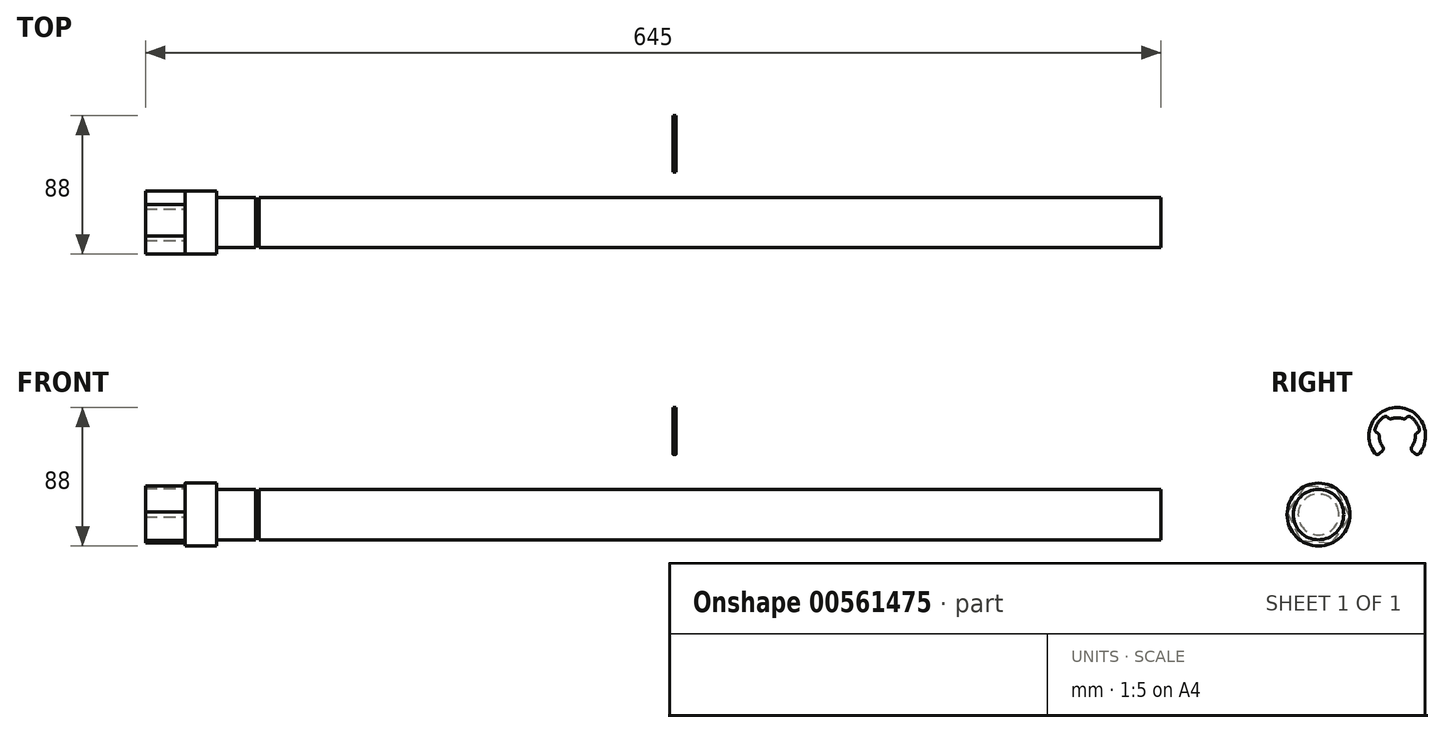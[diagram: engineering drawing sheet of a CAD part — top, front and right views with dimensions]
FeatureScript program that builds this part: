
annotation { "Feature Type Name" : "Feature", "Feature Type Description" : "" }
export const myFeature = defineFeature(function(context is Context, id is Id, definition is map)
    precondition{}
    {
        {
            var Q0;
            Q0=qCreatedBy(makeId("Front.planeOp"),FACE);
            var sketch = newSketch(context, id + "F0", { "sketchPlane" : qUnion([Q0])});
            skLineSegment(sketch, "E0", {"start": v(310, 0) * mm, "end": v(0, 0) * mm});
            skLineSegment(sketch, "E1", {"start": v(0, 0) * mm, "end": v(-310, 0) * mm});
            skLineSegment(sketch, "E2", {"start": v(-310, 0) * mm, "end": v(-310, 20) * mm});
            skLineSegment(sketch, "E3", {"start": v(-310, 20) * mm, "end": v(-290, 20) * mm});
            skLineSegment(sketch, "E4", {"start": v(-290, 20) * mm, "end": v(-290, 16) * mm});
            skLineSegment(sketch, "E5", {"start": v(-290, 16) * mm, "end": v(-265, 16) * mm});
            skLineSegment(sketch, "E6", {"start": v(-265, 16) * mm, "end": v(-265, 13) * mm});
            skLineSegment(sketch, "E7", {"start": v(-265, 13) * mm, "end": v(-263, 13) * mm});
            skLineSegment(sketch, "E8", {"start": v(-263, 13) * mm, "end": v(-263, 16) * mm});
            skLineSegment(sketch, "E9", {"start": v(-263, 16) * mm, "end": v(310, 16) * mm});
            skLineSegment(sketch, "E10", {"start": v(310, 16) * mm, "end": v(310, 0) * mm});
            skLineSegment(sketch, "E11", {"start": v(425.22, 0) * mm, "end": v(-376.8, 0) * mm, "construction": true});
            skPoint(sketch, "E11.startSnap0", {"position": v(155, 0) * mm});
            skSolve(sketch);
        }
        {
            var Q0;
            Q0=makeQuery(id+"F0.imprint","IMPRINT",FACE,{"disambiguationData":[TD([[makeQuery(id+"F0.imprint","IMPRINT",EDGE,{"derivedFrom":sQuery(id+"F0.wireOp",EDGE,"E0")}),-1.0]])]});
            var Q1;
            Q1=sQuery(id+"F0.wireOp",EDGE,"E11");
            revolve(context, id + "F1", {"entities" : qUnion([Q0]), "axis" : qUnion([Q1]), "revolveType" : RevolveType.FULL});
        }
        {
            var Q0;
            Q0=makeQuery(id+"F1.opRevolve","SWEPT_FACE",FACE,{"disambiguationData":[OSD([sQuery(id+"F0.wireOp",EDGE,"E2")])]});
            var sketch = newSketch(context, id + "F2", { "sketchPlane" : qUnion([Q0])});
            skCircle(sketch, "E12.cCircle", {"center": v(0, 0) * mm, "radius": 20 * mm, "construction": true});
            skLineSegment(sketch, "E12.0", {"start": v(11.36, -16.46) * mm, "end": v(-8.58, -18.07) * mm});
            skLineSegment(sketch, "E12.1", {"start": v(-8.58, -18.07) * mm, "end": v(-19.94, -1.6) * mm});
            skLineSegment(sketch, "E12.2", {"start": v(-19.94, -1.6) * mm, "end": v(-11.36, 16.46) * mm});
            skLineSegment(sketch, "E12.3", {"start": v(-11.36, 16.46) * mm, "end": v(8.58, 18.07) * mm});
            skLineSegment(sketch, "E12.4", {"start": v(8.58, 18.07) * mm, "end": v(19.94, 1.6) * mm});
            skLineSegment(sketch, "E12.5", {"start": v(19.94, 1.6) * mm, "end": v(11.36, -16.46) * mm});
            skSolve(sketch);
        }
        {
            var Q0;
            Q0=makeQuery(id+"F2.imprint","IMPRINT",FACE,{"disambiguationData":[TD([[makeQuery(id+"F2.imprint","IMPRINT",EDGE,{"derivedFrom":sQuery(id+"F2.wireOp",EDGE,"E12.0")}),-1.0]])]});
            extrude(context, id + "F3", {"entities" : qUnion([Q0]), "operationType" : NewBodyOperationType.ADD, "depth" : 25 * mm, "offsetDistance" : 25 * mm});
        }
        {
            var Q0;
            Q0=qCreatedBy(makeId("Right.planeOp"),FACE);
            var sketch = newSketch(context, id + "F4", { "sketchPlane" : qUnion([Q0])});
            skArc(sketch, "E13", {"start": v(62.73, 37.27) * mm, "mid": v(50, 68) * mm, "end": v(37.27, 37.27) * mm});
            skArc(sketch, "E14", {"start": v(58.13, 41.87) * mm, "mid": v(60.94, 46.45) * mm, "end": v(61.36, 51.8) * mm});
            skLineSegment(sketch, "E15", {"start": v(50, 50) * mm, "end": v(62.73, 37.27) * mm});
            skLineSegment(sketch, "E16", {"start": v(50, 50) * mm, "end": v(37.27, 37.27) * mm});
            skLineSegment(sketch, "E17", {"start": v(0, 37.27) * mm, "end": v(80.76, 37.27) * mm, "construction": true});
            skCircle(sketch, "E18", {"center": v(50, 50) * mm, "radius": 14.75 * mm});
            skLineSegment(sketch, "E19", {"start": v(50, 50) * mm, "end": v(35.43, 52.3) * mm});
            skLineSegment(sketch, "E20", {"start": v(35.43, 52.3) * mm, "end": v(50, 50) * mm});
            skLineSegment(sketch, "E21", {"start": v(50, 50) * mm, "end": v(43.3, 63.14) * mm});
            skLineSegment(sketch, "E22", {"start": v(50, 50) * mm, "end": v(56.7, 63.14) * mm});
            skLineSegment(sketch, "E23", {"start": v(50, 50) * mm, "end": v(64.57, 52.3) * mm});
            skArc(sketch, "E24.trimOffspring", {"start": v(38.64, 51.8) * mm, "mid": v(39.06, 46.45) * mm, "end": v(41.87, 41.87) * mm});
            skArc(sketch, "E25.trimOffspring", {"start": v(55.22, 60.25) * mm, "mid": v(50, 61.5) * mm, "end": v(44.78, 60.25) * mm});
            skSolve(sketch);
        }
        {
            var Q0;
            {var subQ0=sQuery(id+"F4.wireOp",EDGE,"E14");Q0=makeQuery(id+"F4.imprint","IMPRINT",FACE,{"disambiguationData":[TD([[makeQuery(id+"F4.imprint","IMPRINT",EDGE,{"derivedFrom":subQ0}),-1.0]])]});}
            var Q1;
            {var subQ4=sQuery(id+"F4.wireOp",EDGE,"E13");Q1=makeQuery(id+"F4.imprint","IMPRINT",FACE,{"disambiguationData":[TD([[makeQuery(id+"F4.imprint","IMPRINT",EDGE,{"derivedFrom":subQ4}),1.0]])]});}
            var Q2;
            {var subQ5=sQuery(id+"F4.wireOp",EDGE,"E25.trimOffspring");Q2=makeQuery(id+"F4.imprint","IMPRINT",FACE,{"disambiguationData":[TD([[makeQuery(id+"F4.imprint","IMPRINT",EDGE,{"derivedFrom":subQ5}),-1.0]])]});}
            var Q3;
            {var subQ0=sQuery(id+"F4.wireOp",EDGE,"E24.trimOffspring");Q3=makeQuery(id+"F4.imprint","IMPRINT",FACE,{"disambiguationData":[TD([[makeQuery(id+"F4.imprint","IMPRINT",EDGE,{"derivedFrom":subQ0}),-1.0]])]});}
            extrude(context, id + "F5", {"entities" : qUnion([Q0, Q1, Q2, Q3]), "depth" : 2 * mm, "offsetDistance" : 25 * mm});
        }
        {
            var Q0;
            Q0=makeQuery(id+"F5.opExtrude","SWEPT_EDGE",EDGE,{"disambiguationData":[OSD([sQuery(id+"F4.wireOp",EDGE,"E22"),sQuery(id+"F4.wireOp",EDGE,"E25.trimOffspring")])]});
            var Q1;
            Q1=makeQuery(id+"F5.opExtrude","SWEPT_EDGE",EDGE,{"disambiguationData":[OSD([sQuery(id+"F4.wireOp",EDGE,"E21"),sQuery(id+"F4.wireOp",EDGE,"E25.trimOffspring")])]});
            var Q2;
            Q2=makeQuery(id+"F5.opExtrude","SWEPT_EDGE",EDGE,{"disambiguationData":[OSD([sQuery(id+"F4.wireOp",EDGE,"E13"),sQuery(id+"F4.wireOp",EDGE,"E15")])]});
            var Q3;
            Q3=makeQuery(id+"F5.opExtrude","SWEPT_EDGE",EDGE,{"disambiguationData":[OSD([sQuery(id+"F4.wireOp",EDGE,"E14"),sQuery(id+"F4.wireOp",EDGE,"E15")])]});
            var Q4;
            Q4=makeQuery(id+"F5.opExtrude","SWEPT_EDGE",EDGE,{"disambiguationData":[OSD([sQuery(id+"F4.wireOp",EDGE,"E16"),sQuery(id+"F4.wireOp",EDGE,"E24.trimOffspring")])]});
            var Q5;
            Q5=makeQuery(id+"F5.opExtrude","SWEPT_EDGE",EDGE,{"disambiguationData":[OSD([sQuery(id+"F4.wireOp",EDGE,"E13"),sQuery(id+"F4.wireOp",EDGE,"E16")])]});
            var Q6;
            Q6=makeQuery(id+"F5.opExtrude","SWEPT_EDGE",EDGE,{"disambiguationData":[OSD([sQuery(id+"F4.wireOp",EDGE,"E14"),sQuery(id+"F4.wireOp",EDGE,"E23")])]});
            var Q7;
            Q7=makeQuery(id+"F5.opExtrude","SWEPT_EDGE",EDGE,{"disambiguationData":[OSD([sQuery(id+"F4.wireOp",EDGE,"E20"),sQuery(id+"F4.wireOp",EDGE,"E24.trimOffspring")])]});
            fillet(context, id + "F6", {"entities" : qUnion([Q0, Q1, Q2, Q3, Q4, Q5, Q6, Q7]), "radius" : 2 * mm, "tangentPropagation" : true, "allowEdgeOverflow" : false});
        }
        {
            var Q0;
            Q0=makeQuery(id+"F5.opExtrude","SWEPT_EDGE",EDGE,{"disambiguationData":[OSD([sQuery(id+"F4.wireOp",EDGE,"E18"),sQuery(id+"F4.wireOp",EDGE,"E22")])]});
            var Q1;
            Q1=makeQuery(id+"F5.opExtrude","SWEPT_EDGE",EDGE,{"disambiguationData":[OSD([sQuery(id+"F4.wireOp",EDGE,"E18"),sQuery(id+"F4.wireOp",EDGE,"E21")])]});
            var Q2;
            Q2=makeQuery(id+"F5.opExtrude","SWEPT_EDGE",EDGE,{"disambiguationData":[OSD([sQuery(id+"F4.wireOp",EDGE,"E18"),sQuery(id+"F4.wireOp",EDGE,"E23")])]});
            var Q3;
            Q3=makeQuery(id+"F5.opExtrude","SWEPT_EDGE",EDGE,{"disambiguationData":[OSD([sQuery(id+"F4.wireOp",EDGE,"E18"),sQuery(id+"F4.wireOp",EDGE,"E20")])]});
            fillet(context, id + "F7", {"entities" : qUnion([Q0, Q1, Q2, Q3]), "radius" : 2 * mm, "tangentPropagation" : true, "allowEdgeOverflow" : false});
        }
    });
